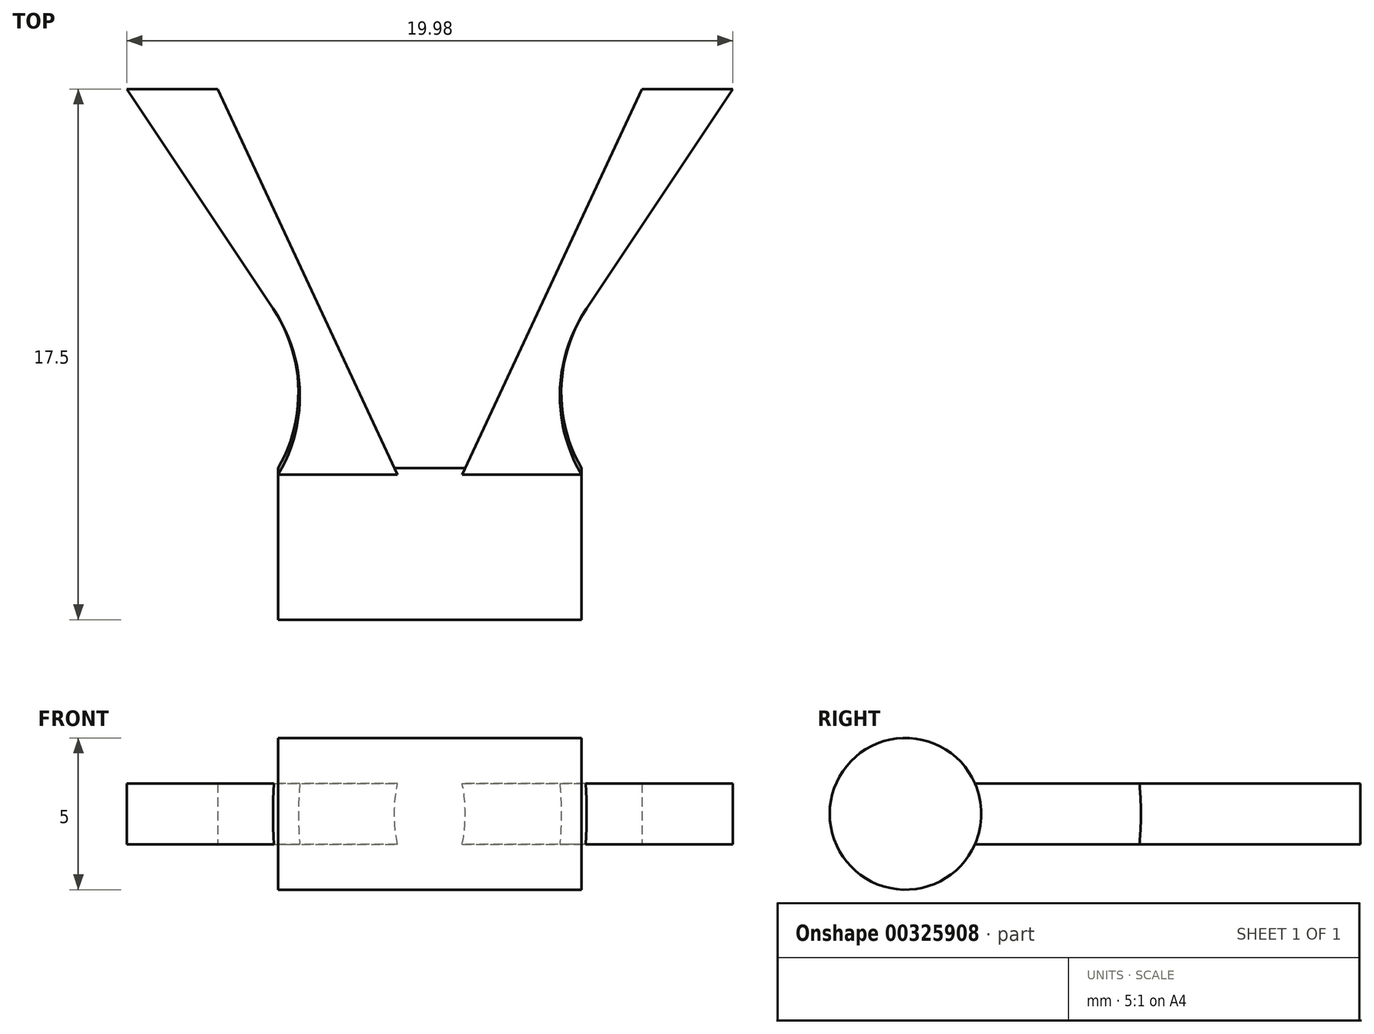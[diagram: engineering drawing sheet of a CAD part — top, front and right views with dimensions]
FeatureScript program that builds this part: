
annotation { "Feature Type Name" : "Feature", "Feature Type Description" : "" }
export const myFeature = defineFeature(function(context is Context, id is Id, definition is map)
    precondition{}
    {
        {
            var Q0;
            Q0=qCreatedBy(makeId("Top.planeOp"),FACE);
            var sketch = newSketch(context, id + "F0", { "sketchPlane" : qUnion([Q0])});
            skLineSegment(sketch, "E0.bottom", {"start": v(-5, 0) * mm, "end": v(5, 0) * mm});
            skLineSegment(sketch, "E0.top", {"start": v(-5, 2.5) * mm, "end": v(5, 2.5) * mm});
            skLineSegment(sketch, "E0.left", {"start": v(-5, 0) * mm, "end": v(-5, 2.5) * mm});
            skLineSegment(sketch, "E0.right", {"start": v(5, 0) * mm, "end": v(5, 2.5) * mm});
            skSolve(sketch);
        }
        {
            var Q0;
            Q0=makeQuery(id+"F0.imprint","IMPRINT",FACE,{"disambiguationData":[TD([[makeQuery(id+"F0.imprint","IMPRINT",EDGE,{"derivedFrom":sQuery(id+"F0.wireOp",EDGE,"E0.bottom")}),1.0]])]});
            var Q1;
            Q1=sQuery(id+"F0.wireOp",EDGE,"E0.bottom");
            revolve(context, id + "F1", {"entities" : qUnion([Q0]), "axis" : qUnion([Q1]), "revolveType" : RevolveType.FULL});
        }
        {
            var Q0;
            Q0=qCreatedBy(makeId("Top.planeOp"),FACE);
            var sketch = newSketch(context, id + "F2", { "sketchPlane" : qUnion([Q0])});
            skLineSegment(sketch, "E1", {"start": v(0, 0) * mm, "end": v(-10, 15) * mm});
            skLineSegment(sketch, "E2", {"start": v(-10, 15) * mm, "end": v(-7, 15) * mm});
            skLineSegment(sketch, "E3", {"start": v(-7, 15) * mm, "end": v(0, 0) * mm});
            skLineSegment(sketch, "E4", {"start": v(0, 0) * mm, "end": v(-12.86, 0) * mm, "construction": true});
            skSolve(sketch);
        }
        {
            var Q0;
            Q0=makeQuery(id+"F2.imprint","IMPRINT",FACE,{"disambiguationData":[TD([[makeQuery(id+"F2.imprint","IMPRINT",EDGE,{"derivedFrom":sQuery(id+"F2.wireOp",EDGE,"E1")}),-1.0]])]});
            extrude(context, id + "F3", {"entities" : qUnion([Q0]), "operationType" : NewBodyOperationType.ADD, "endBound" : BoundingType.SYMMETRIC, "depth" : 2 * mm});
        }
        {
            var Q0;
            Q0=makeQuery(id+"F3.boolean.opBoolean","INTERSECT",EDGE,{"derivedFrom":[makeQuery(id+"F1.opRevolve","SWEPT_FACE",FACE,{"disambiguationData":[OSD([sQuery(id+"F0.wireOp",EDGE,"E0.top")])]}),makeQuery(id+"F3.opExtrude","SWEPT_FACE",FACE,{"disambiguationData":[OSD([sQuery(id+"F2.wireOp",EDGE,"E1")])]})]});
            fillet(context, id + "F4", {"entities" : qUnion([Q0]), "radius" : 5 * mm, "tangentPropagation" : true, "allowEdgeOverflow" : false});
        }
        {
            var Q0;
            Q0=makeQuery(id+"F1.opRevolve","SWEPT_BODY",BODY,{"disambiguationData":[OSD([sQuery(id+"F0.wireOp",EDGE,"E0.bottom"),sQuery(id+"F0.wireOp",EDGE,"E0.top"),sQuery(id+"F0.wireOp",EDGE,"E0.left"),sQuery(id+"F0.wireOp",EDGE,"E0.right")])]});
            var Q1;
            Q1=qCreatedBy(makeId("Right.planeOp"),FACE);
            mirror(context, id + "F5", {"operationType" : NewBodyOperationType.ADD, "entities" : qUnion([Q0]), "mirrorPlane" : qUnion([Q1])});
        }
    });
